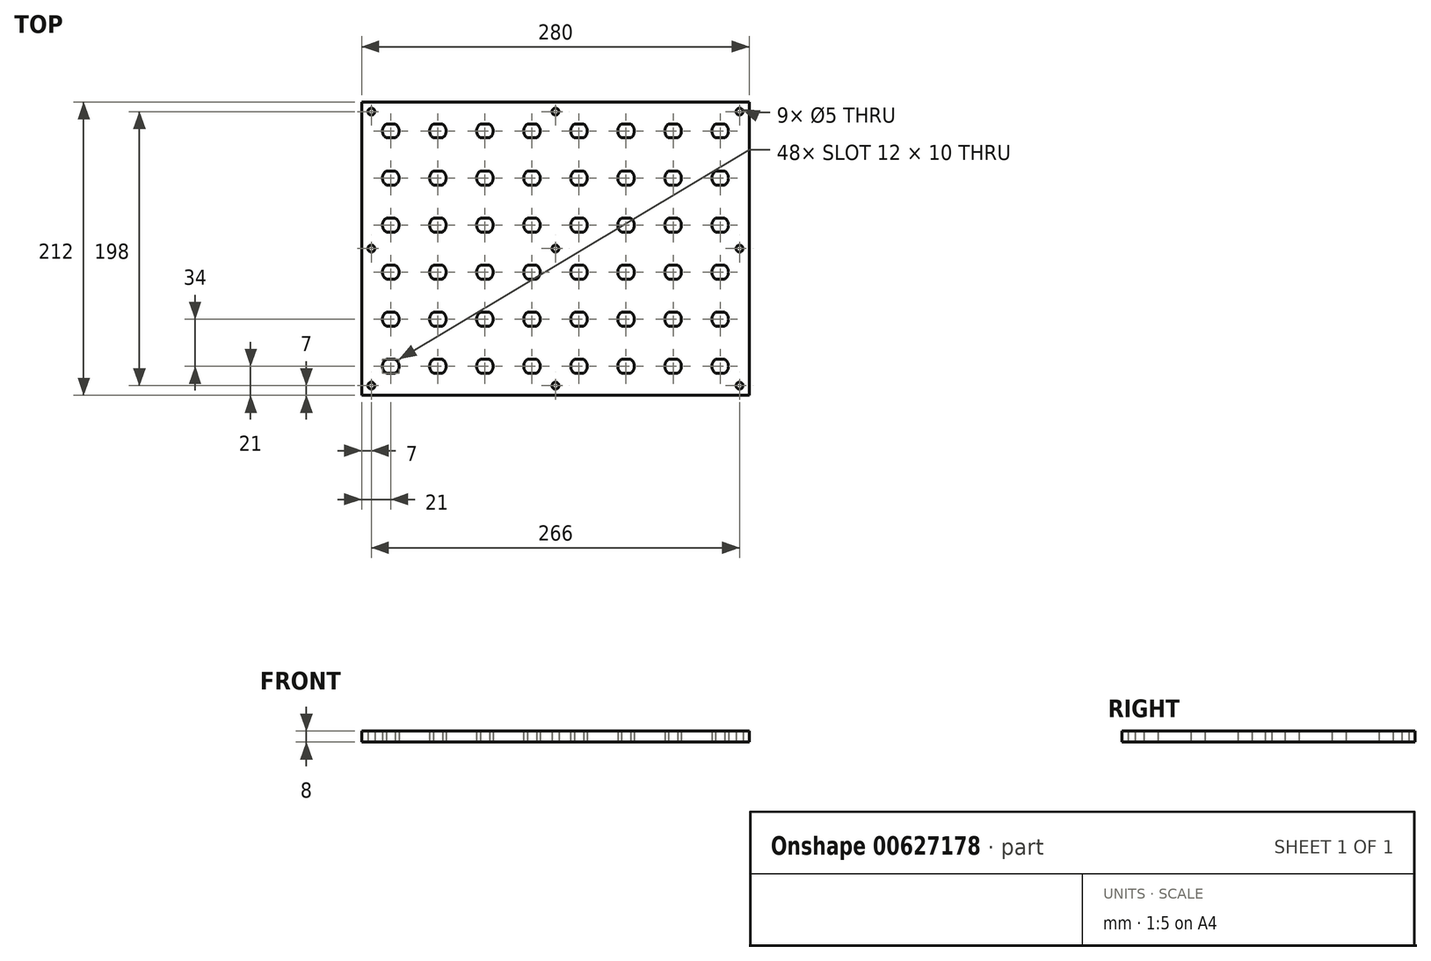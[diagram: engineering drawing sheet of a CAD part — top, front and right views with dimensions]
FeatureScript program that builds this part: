
annotation { "Feature Type Name" : "Feature", "Feature Type Description" : "" }
export const myFeature = defineFeature(function(context is Context, id is Id, definition is map)
    precondition{}
    {
        {
            var Q0;
            Q0=qCreatedBy(makeId("Top.planeOp"),FACE);
            var sketch = newSketch(context, id + "F0", { "sketchPlane" : qUnion([Q0])});
            skLineSegment(sketch, "E0.bottom", {"start": v(-140, -106) * mm, "end": v(140, -106) * mm});
            skLineSegment(sketch, "E0.top", {"start": v(-140, 106) * mm, "end": v(140, 106) * mm});
            skLineSegment(sketch, "E0.left", {"start": v(-140, -106) * mm, "end": v(-140, 106) * mm});
            skLineSegment(sketch, "E0.right", {"start": v(140, -106) * mm, "end": v(140, 106) * mm});
            skPoint(sketch, "E0.middle", {"position": v(0, 0) * mm});
            skLineSegment(sketch, "E1", {"start": v(-102, 141.86) * mm, "end": v(-102, -178.14) * mm, "construction": true});
            skLineSegment(sketch, "E2", {"start": v(-122.32, -80) * mm, "end": v(-115.68, -80) * mm});
            skLineSegment(sketch, "E3", {"start": v(-122.32, -90) * mm, "end": v(-115.68, -90) * mm});
            skArc(sketch, "E4", {"start": v(-122.32, -80) * mm, "mid": v(-125, -85) * mm, "end": v(-122.32, -90) * mm});
            skArc(sketch, "E5", {"start": v(-115.68, -90) * mm, "mid": v(-113, -85) * mm, "end": v(-115.68, -80) * mm});
            skLineSegment(sketch, "E6", {"start": v(-165.76, -85) * mm, "end": v(184.24, -85) * mm, "construction": true});
            skLineSegment(sketch, "E7.0.1.0", {"start": v(-165.76, -51) * mm, "end": v(184.24, -51) * mm, "construction": true});
            skArc(sketch, "E7.0.1.1", {"start": v(-122.32, -46) * mm, "mid": v(-125, -51) * mm, "end": v(-122.32, -56) * mm});
            skLineSegment(sketch, "E7.0.1.2", {"start": v(-122.32, -56) * mm, "end": v(-115.68, -56) * mm});
            skLineSegment(sketch, "E7.0.1.3", {"start": v(-122.32, -46) * mm, "end": v(-115.68, -46) * mm});
            skArc(sketch, "E7.0.1.4", {"start": v(-115.68, -56) * mm, "mid": v(-113, -51) * mm, "end": v(-115.68, -46) * mm});
            skLineSegment(sketch, "E7.0.2.0", {"start": v(-165.76, -17) * mm, "end": v(184.24, -17) * mm, "construction": true});
            skArc(sketch, "E7.0.2.1", {"start": v(-122.32, -12) * mm, "mid": v(-125, -17) * mm, "end": v(-122.32, -22) * mm});
            skLineSegment(sketch, "E7.0.2.2", {"start": v(-122.32, -22) * mm, "end": v(-115.68, -22) * mm});
            skLineSegment(sketch, "E7.0.2.3", {"start": v(-122.32, -12) * mm, "end": v(-115.68, -12) * mm});
            skArc(sketch, "E7.0.2.4", {"start": v(-115.68, -22) * mm, "mid": v(-113, -17) * mm, "end": v(-115.68, -12) * mm});
            skLineSegment(sketch, "E7.0.3.0", {"start": v(-165.76, 17) * mm, "end": v(184.24, 17) * mm, "construction": true});
            skArc(sketch, "E7.0.3.1", {"start": v(-122.32, 22) * mm, "mid": v(-125, 17) * mm, "end": v(-122.32, 12) * mm});
            skLineSegment(sketch, "E7.0.3.2", {"start": v(-122.32, 12) * mm, "end": v(-115.68, 12) * mm});
            skLineSegment(sketch, "E7.0.3.3", {"start": v(-122.32, 22) * mm, "end": v(-115.68, 22) * mm});
            skArc(sketch, "E7.0.3.4", {"start": v(-115.68, 12) * mm, "mid": v(-113, 17) * mm, "end": v(-115.68, 22) * mm});
            skLineSegment(sketch, "E7.0.4.0", {"start": v(-165.76, 51) * mm, "end": v(184.24, 51) * mm, "construction": true});
            skArc(sketch, "E7.0.4.1", {"start": v(-122.32, 56) * mm, "mid": v(-125, 51) * mm, "end": v(-122.32, 46) * mm});
            skLineSegment(sketch, "E7.0.4.2", {"start": v(-122.32, 46) * mm, "end": v(-115.68, 46) * mm});
            skLineSegment(sketch, "E7.0.4.3", {"start": v(-122.32, 56) * mm, "end": v(-115.68, 56) * mm});
            skArc(sketch, "E7.0.4.4", {"start": v(-115.68, 46) * mm, "mid": v(-113, 51) * mm, "end": v(-115.68, 56) * mm});
            skLineSegment(sketch, "E7.1.0.0", {"start": v(-131.76, -85) * mm, "end": v(218.24, -85) * mm, "construction": true});
            skArc(sketch, "E7.1.0.1", {"start": v(-88.32, -80) * mm, "mid": v(-91, -85) * mm, "end": v(-88.32, -90) * mm});
            skLineSegment(sketch, "E7.1.0.2", {"start": v(-88.32, -90) * mm, "end": v(-81.68, -90) * mm});
            skLineSegment(sketch, "E7.1.0.3", {"start": v(-88.32, -80) * mm, "end": v(-81.68, -80) * mm});
            skArc(sketch, "E7.1.0.4", {"start": v(-81.68, -90) * mm, "mid": v(-79, -85) * mm, "end": v(-81.68, -80) * mm});
            skLineSegment(sketch, "E7.1.1.0", {"start": v(-131.76, -51) * mm, "end": v(218.24, -51) * mm, "construction": true});
            skArc(sketch, "E7.1.1.1", {"start": v(-88.32, -46) * mm, "mid": v(-91, -51) * mm, "end": v(-88.32, -56) * mm});
            skLineSegment(sketch, "E7.1.1.2", {"start": v(-88.32, -56) * mm, "end": v(-81.68, -56) * mm});
            skLineSegment(sketch, "E7.1.1.3", {"start": v(-88.32, -46) * mm, "end": v(-81.68, -46) * mm});
            skArc(sketch, "E7.1.1.4", {"start": v(-81.68, -56) * mm, "mid": v(-79, -51) * mm, "end": v(-81.68, -46) * mm});
            skLineSegment(sketch, "E7.1.2.0", {"start": v(-131.76, -17) * mm, "end": v(218.24, -17) * mm, "construction": true});
            skArc(sketch, "E7.1.2.1", {"start": v(-88.32, -12) * mm, "mid": v(-91, -17) * mm, "end": v(-88.32, -22) * mm});
            skLineSegment(sketch, "E7.1.2.2", {"start": v(-88.32, -22) * mm, "end": v(-81.68, -22) * mm});
            skLineSegment(sketch, "E7.1.2.3", {"start": v(-88.32, -12) * mm, "end": v(-81.68, -12) * mm});
            skArc(sketch, "E7.1.2.4", {"start": v(-81.68, -22) * mm, "mid": v(-79, -17) * mm, "end": v(-81.68, -12) * mm});
            skLineSegment(sketch, "E7.1.3.0", {"start": v(-131.76, 17) * mm, "end": v(218.24, 17) * mm, "construction": true});
            skArc(sketch, "E7.1.3.1", {"start": v(-88.32, 22) * mm, "mid": v(-91, 17) * mm, "end": v(-88.32, 12) * mm});
            skLineSegment(sketch, "E7.1.3.2", {"start": v(-88.32, 12) * mm, "end": v(-81.68, 12) * mm});
            skLineSegment(sketch, "E7.1.3.3", {"start": v(-88.32, 22) * mm, "end": v(-81.68, 22) * mm});
            skArc(sketch, "E7.1.3.4", {"start": v(-81.68, 12) * mm, "mid": v(-79, 17) * mm, "end": v(-81.68, 22) * mm});
            skLineSegment(sketch, "E7.1.4.0", {"start": v(-131.76, 51) * mm, "end": v(218.24, 51) * mm, "construction": true});
            skArc(sketch, "E7.1.4.1", {"start": v(-88.32, 56) * mm, "mid": v(-91, 51) * mm, "end": v(-88.32, 46) * mm});
            skLineSegment(sketch, "E7.1.4.2", {"start": v(-88.32, 46) * mm, "end": v(-81.68, 46) * mm});
            skLineSegment(sketch, "E7.1.4.3", {"start": v(-88.32, 56) * mm, "end": v(-81.68, 56) * mm});
            skArc(sketch, "E7.1.4.4", {"start": v(-81.68, 46) * mm, "mid": v(-79, 51) * mm, "end": v(-81.68, 56) * mm});
            skLineSegment(sketch, "E7.2.0.0", {"start": v(-97.76, -85) * mm, "end": v(252.24, -85) * mm, "construction": true});
            skArc(sketch, "E7.2.0.1", {"start": v(-54.32, -80) * mm, "mid": v(-57, -85) * mm, "end": v(-54.32, -90) * mm});
            skLineSegment(sketch, "E7.2.0.2", {"start": v(-54.32, -90) * mm, "end": v(-47.68, -90) * mm});
            skLineSegment(sketch, "E7.2.0.3", {"start": v(-54.32, -80) * mm, "end": v(-47.68, -80) * mm});
            skArc(sketch, "E7.2.0.4", {"start": v(-47.68, -90) * mm, "mid": v(-45, -85) * mm, "end": v(-47.68, -80) * mm});
            skLineSegment(sketch, "E7.2.1.0", {"start": v(-97.76, -51) * mm, "end": v(252.24, -51) * mm, "construction": true});
            skArc(sketch, "E7.2.1.1", {"start": v(-54.32, -46) * mm, "mid": v(-57, -51) * mm, "end": v(-54.32, -56) * mm});
            skLineSegment(sketch, "E7.2.1.2", {"start": v(-54.32, -56) * mm, "end": v(-47.68, -56) * mm});
            skLineSegment(sketch, "E7.2.1.3", {"start": v(-54.32, -46) * mm, "end": v(-47.68, -46) * mm});
            skArc(sketch, "E7.2.1.4", {"start": v(-47.68, -56) * mm, "mid": v(-45, -51) * mm, "end": v(-47.68, -46) * mm});
            skLineSegment(sketch, "E7.2.2.0", {"start": v(-97.76, -17) * mm, "end": v(252.24, -17) * mm, "construction": true});
            skArc(sketch, "E7.2.2.1", {"start": v(-54.32, -12) * mm, "mid": v(-57, -17) * mm, "end": v(-54.32, -22) * mm});
            skLineSegment(sketch, "E7.2.2.2", {"start": v(-54.32, -22) * mm, "end": v(-47.68, -22) * mm});
            skLineSegment(sketch, "E7.2.2.3", {"start": v(-54.32, -12) * mm, "end": v(-47.68, -12) * mm});
            skArc(sketch, "E7.2.2.4", {"start": v(-47.68, -22) * mm, "mid": v(-45, -17) * mm, "end": v(-47.68, -12) * mm});
            skLineSegment(sketch, "E7.2.3.0", {"start": v(-97.76, 17) * mm, "end": v(252.24, 17) * mm, "construction": true});
            skArc(sketch, "E7.2.3.1", {"start": v(-54.32, 22) * mm, "mid": v(-57, 17) * mm, "end": v(-54.32, 12) * mm});
            skLineSegment(sketch, "E7.2.3.2", {"start": v(-54.32, 12) * mm, "end": v(-47.68, 12) * mm});
            skLineSegment(sketch, "E7.2.3.3", {"start": v(-54.32, 22) * mm, "end": v(-47.68, 22) * mm});
            skArc(sketch, "E7.2.3.4", {"start": v(-47.68, 12) * mm, "mid": v(-45, 17) * mm, "end": v(-47.68, 22) * mm});
            skLineSegment(sketch, "E7.2.4.0", {"start": v(-97.76, 51) * mm, "end": v(252.24, 51) * mm, "construction": true});
            skArc(sketch, "E7.2.4.1", {"start": v(-54.32, 56) * mm, "mid": v(-57, 51) * mm, "end": v(-54.32, 46) * mm});
            skLineSegment(sketch, "E7.2.4.2", {"start": v(-54.32, 46) * mm, "end": v(-47.68, 46) * mm});
            skLineSegment(sketch, "E7.2.4.3", {"start": v(-54.32, 56) * mm, "end": v(-47.68, 56) * mm});
            skArc(sketch, "E7.2.4.4", {"start": v(-47.68, 46) * mm, "mid": v(-45, 51) * mm, "end": v(-47.68, 56) * mm});
            skLineSegment(sketch, "E7.3.0.0", {"start": v(-63.76, -85) * mm, "end": v(286.24, -85) * mm, "construction": true});
            skArc(sketch, "E7.3.0.1", {"start": v(-20.32, -80) * mm, "mid": v(-23, -85) * mm, "end": v(-20.32, -90) * mm});
            skLineSegment(sketch, "E7.3.0.2", {"start": v(-20.32, -90) * mm, "end": v(-13.68, -90) * mm});
            skLineSegment(sketch, "E7.3.0.3", {"start": v(-20.32, -80) * mm, "end": v(-13.68, -80) * mm});
            skArc(sketch, "E7.3.0.4", {"start": v(-13.68, -90) * mm, "mid": v(-11, -85) * mm, "end": v(-13.68, -80) * mm});
            skLineSegment(sketch, "E7.3.1.0", {"start": v(-63.76, -51) * mm, "end": v(286.24, -51) * mm, "construction": true});
            skArc(sketch, "E7.3.1.1", {"start": v(-20.32, -46) * mm, "mid": v(-23, -51) * mm, "end": v(-20.32, -56) * mm});
            skLineSegment(sketch, "E7.3.1.2", {"start": v(-20.32, -56) * mm, "end": v(-13.68, -56) * mm});
            skLineSegment(sketch, "E7.3.1.3", {"start": v(-20.32, -46) * mm, "end": v(-13.68, -46) * mm});
            skArc(sketch, "E7.3.1.4", {"start": v(-13.68, -56) * mm, "mid": v(-11, -51) * mm, "end": v(-13.68, -46) * mm});
            skLineSegment(sketch, "E7.3.2.0", {"start": v(-63.76, -17) * mm, "end": v(286.24, -17) * mm, "construction": true});
            skArc(sketch, "E7.3.2.1", {"start": v(-20.32, -12) * mm, "mid": v(-23, -17) * mm, "end": v(-20.32, -22) * mm});
            skLineSegment(sketch, "E7.3.2.2", {"start": v(-20.32, -22) * mm, "end": v(-13.68, -22) * mm});
            skLineSegment(sketch, "E7.3.2.3", {"start": v(-20.32, -12) * mm, "end": v(-13.68, -12) * mm});
            skArc(sketch, "E7.3.2.4", {"start": v(-13.68, -22) * mm, "mid": v(-11, -17) * mm, "end": v(-13.68, -12) * mm});
            skLineSegment(sketch, "E7.3.3.0", {"start": v(-63.76, 17) * mm, "end": v(286.24, 17) * mm, "construction": true});
            skArc(sketch, "E7.3.3.1", {"start": v(-20.32, 22) * mm, "mid": v(-23, 17) * mm, "end": v(-20.32, 12) * mm});
            skLineSegment(sketch, "E7.3.3.2", {"start": v(-20.32, 12) * mm, "end": v(-13.68, 12) * mm});
            skLineSegment(sketch, "E7.3.3.3", {"start": v(-20.32, 22) * mm, "end": v(-13.68, 22) * mm});
            skArc(sketch, "E7.3.3.4", {"start": v(-13.68, 12) * mm, "mid": v(-11, 17) * mm, "end": v(-13.68, 22) * mm});
            skLineSegment(sketch, "E7.3.4.0", {"start": v(-63.76, 51) * mm, "end": v(286.24, 51) * mm, "construction": true});
            skArc(sketch, "E7.3.4.1", {"start": v(-20.32, 56) * mm, "mid": v(-23, 51) * mm, "end": v(-20.32, 46) * mm});
            skLineSegment(sketch, "E7.3.4.2", {"start": v(-20.32, 46) * mm, "end": v(-13.68, 46) * mm});
            skLineSegment(sketch, "E7.3.4.3", {"start": v(-20.32, 56) * mm, "end": v(-13.68, 56) * mm});
            skArc(sketch, "E7.3.4.4", {"start": v(-13.68, 46) * mm, "mid": v(-11, 51) * mm, "end": v(-13.68, 56) * mm});
            skLineSegment(sketch, "E7.4.0.0", {"start": v(-29.76, -85) * mm, "end": v(320.24, -85) * mm, "construction": true});
            skArc(sketch, "E7.4.0.1", {"start": v(13.68, -80) * mm, "mid": v(11, -85) * mm, "end": v(13.68, -90) * mm});
            skLineSegment(sketch, "E7.4.0.2", {"start": v(13.68, -90) * mm, "end": v(20.32, -90) * mm});
            skLineSegment(sketch, "E7.4.0.3", {"start": v(13.68, -80) * mm, "end": v(20.32, -80) * mm});
            skArc(sketch, "E7.4.0.4", {"start": v(20.32, -90) * mm, "mid": v(23, -85) * mm, "end": v(20.32, -80) * mm});
            skLineSegment(sketch, "E7.4.1.0", {"start": v(-29.76, -51) * mm, "end": v(320.24, -51) * mm, "construction": true});
            skArc(sketch, "E7.4.1.1", {"start": v(13.68, -46) * mm, "mid": v(11, -51) * mm, "end": v(13.68, -56) * mm});
            skLineSegment(sketch, "E7.4.1.2", {"start": v(13.68, -56) * mm, "end": v(20.32, -56) * mm});
            skLineSegment(sketch, "E7.4.1.3", {"start": v(13.68, -46) * mm, "end": v(20.32, -46) * mm});
            skArc(sketch, "E7.4.1.4", {"start": v(20.32, -56) * mm, "mid": v(23, -51) * mm, "end": v(20.32, -46) * mm});
            skLineSegment(sketch, "E7.4.2.0", {"start": v(-29.76, -17) * mm, "end": v(320.24, -17) * mm, "construction": true});
            skArc(sketch, "E7.4.2.1", {"start": v(13.68, -12) * mm, "mid": v(11, -17) * mm, "end": v(13.68, -22) * mm});
            skLineSegment(sketch, "E7.4.2.2", {"start": v(13.68, -22) * mm, "end": v(20.32, -22) * mm});
            skLineSegment(sketch, "E7.4.2.3", {"start": v(13.68, -12) * mm, "end": v(20.32, -12) * mm});
            skArc(sketch, "E7.4.2.4", {"start": v(20.32, -22) * mm, "mid": v(23, -17) * mm, "end": v(20.32, -12) * mm});
            skLineSegment(sketch, "E7.4.3.0", {"start": v(-29.76, 17) * mm, "end": v(320.24, 17) * mm, "construction": true});
            skArc(sketch, "E7.4.3.1", {"start": v(13.68, 22) * mm, "mid": v(11, 17) * mm, "end": v(13.68, 12) * mm});
            skLineSegment(sketch, "E7.4.3.2", {"start": v(13.68, 12) * mm, "end": v(20.32, 12) * mm});
            skLineSegment(sketch, "E7.4.3.3", {"start": v(13.68, 22) * mm, "end": v(20.32, 22) * mm});
            skArc(sketch, "E7.4.3.4", {"start": v(20.32, 12) * mm, "mid": v(23, 17) * mm, "end": v(20.32, 22) * mm});
            skLineSegment(sketch, "E7.4.4.0", {"start": v(-29.76, 51) * mm, "end": v(320.24, 51) * mm, "construction": true});
            skArc(sketch, "E7.4.4.1", {"start": v(13.68, 56) * mm, "mid": v(11, 51) * mm, "end": v(13.68, 46) * mm});
            skLineSegment(sketch, "E7.4.4.2", {"start": v(13.68, 46) * mm, "end": v(20.32, 46) * mm});
            skLineSegment(sketch, "E7.4.4.3", {"start": v(13.68, 56) * mm, "end": v(20.32, 56) * mm});
            skArc(sketch, "E7.4.4.4", {"start": v(20.32, 46) * mm, "mid": v(23, 51) * mm, "end": v(20.32, 56) * mm});
            skLineSegment(sketch, "E7.5.0.0", {"start": v(4.24, -85) * mm, "end": v(354.24, -85) * mm, "construction": true});
            skArc(sketch, "E7.5.0.1", {"start": v(47.68, -80) * mm, "mid": v(45, -85) * mm, "end": v(47.68, -90) * mm});
            skLineSegment(sketch, "E7.5.0.2", {"start": v(47.68, -90) * mm, "end": v(54.32, -90) * mm});
            skLineSegment(sketch, "E7.5.0.3", {"start": v(47.68, -80) * mm, "end": v(54.32, -80) * mm});
            skArc(sketch, "E7.5.0.4", {"start": v(54.32, -90) * mm, "mid": v(57, -85) * mm, "end": v(54.32, -80) * mm});
            skLineSegment(sketch, "E7.5.1.0", {"start": v(4.24, -51) * mm, "end": v(354.24, -51) * mm, "construction": true});
            skArc(sketch, "E7.5.1.1", {"start": v(47.68, -46) * mm, "mid": v(45, -51) * mm, "end": v(47.68, -56) * mm});
            skLineSegment(sketch, "E7.5.1.2", {"start": v(47.68, -56) * mm, "end": v(54.32, -56) * mm});
            skLineSegment(sketch, "E7.5.1.3", {"start": v(47.68, -46) * mm, "end": v(54.32, -46) * mm});
            skArc(sketch, "E7.5.1.4", {"start": v(54.32, -56) * mm, "mid": v(57, -51) * mm, "end": v(54.32, -46) * mm});
            skLineSegment(sketch, "E7.5.2.0", {"start": v(4.24, -17) * mm, "end": v(354.24, -17) * mm, "construction": true});
            skArc(sketch, "E7.5.2.1", {"start": v(47.68, -12) * mm, "mid": v(45, -17) * mm, "end": v(47.68, -22) * mm});
            skLineSegment(sketch, "E7.5.2.2", {"start": v(47.68, -22) * mm, "end": v(54.32, -22) * mm});
            skLineSegment(sketch, "E7.5.2.3", {"start": v(47.68, -12) * mm, "end": v(54.32, -12) * mm});
            skArc(sketch, "E7.5.2.4", {"start": v(54.32, -22) * mm, "mid": v(57, -17) * mm, "end": v(54.32, -12) * mm});
            skLineSegment(sketch, "E7.5.3.0", {"start": v(4.24, 17) * mm, "end": v(354.24, 17) * mm, "construction": true});
            skArc(sketch, "E7.5.3.1", {"start": v(47.68, 22) * mm, "mid": v(45, 17) * mm, "end": v(47.68, 12) * mm});
            skLineSegment(sketch, "E7.5.3.2", {"start": v(47.68, 12) * mm, "end": v(54.32, 12) * mm});
            skLineSegment(sketch, "E7.5.3.3", {"start": v(47.68, 22) * mm, "end": v(54.32, 22) * mm});
            skArc(sketch, "E7.5.3.4", {"start": v(54.32, 12) * mm, "mid": v(57, 17) * mm, "end": v(54.32, 22) * mm});
            skLineSegment(sketch, "E7.5.4.0", {"start": v(4.24, 51) * mm, "end": v(354.24, 51) * mm, "construction": true});
            skArc(sketch, "E7.5.4.1", {"start": v(47.68, 56) * mm, "mid": v(45, 51) * mm, "end": v(47.68, 46) * mm});
            skLineSegment(sketch, "E7.5.4.2", {"start": v(47.68, 46) * mm, "end": v(54.32, 46) * mm});
            skLineSegment(sketch, "E7.5.4.3", {"start": v(47.68, 56) * mm, "end": v(54.32, 56) * mm});
            skArc(sketch, "E7.5.4.4", {"start": v(54.32, 46) * mm, "mid": v(57, 51) * mm, "end": v(54.32, 56) * mm});
            skLineSegment(sketch, "E7.6.0.0", {"start": v(38.24, -85) * mm, "end": v(388.24, -85) * mm, "construction": true});
            skArc(sketch, "E7.6.0.1", {"start": v(81.68, -80) * mm, "mid": v(79, -85) * mm, "end": v(81.68, -90) * mm});
            skLineSegment(sketch, "E7.6.0.2", {"start": v(81.68, -90) * mm, "end": v(88.32, -90) * mm});
            skLineSegment(sketch, "E7.6.0.3", {"start": v(81.68, -80) * mm, "end": v(88.32, -80) * mm});
            skArc(sketch, "E7.6.0.4", {"start": v(88.32, -90) * mm, "mid": v(91, -85) * mm, "end": v(88.32, -80) * mm});
            skLineSegment(sketch, "E7.6.1.0", {"start": v(38.24, -51) * mm, "end": v(388.24, -51) * mm, "construction": true});
            skArc(sketch, "E7.6.1.1", {"start": v(81.68, -46) * mm, "mid": v(79, -51) * mm, "end": v(81.68, -56) * mm});
            skLineSegment(sketch, "E7.6.1.2", {"start": v(81.68, -56) * mm, "end": v(88.32, -56) * mm});
            skLineSegment(sketch, "E7.6.1.3", {"start": v(81.68, -46) * mm, "end": v(88.32, -46) * mm});
            skArc(sketch, "E7.6.1.4", {"start": v(88.32, -56) * mm, "mid": v(91, -51) * mm, "end": v(88.32, -46) * mm});
            skLineSegment(sketch, "E7.6.2.0", {"start": v(38.24, -17) * mm, "end": v(388.24, -17) * mm, "construction": true});
            skArc(sketch, "E7.6.2.1", {"start": v(81.68, -12) * mm, "mid": v(79, -17) * mm, "end": v(81.68, -22) * mm});
            skLineSegment(sketch, "E7.6.2.2", {"start": v(81.68, -22) * mm, "end": v(88.32, -22) * mm});
            skLineSegment(sketch, "E7.6.2.3", {"start": v(81.68, -12) * mm, "end": v(88.32, -12) * mm});
            skArc(sketch, "E7.6.2.4", {"start": v(88.32, -22) * mm, "mid": v(91, -17) * mm, "end": v(88.32, -12) * mm});
            skLineSegment(sketch, "E7.6.3.0", {"start": v(38.24, 17) * mm, "end": v(388.24, 17) * mm, "construction": true});
            skArc(sketch, "E7.6.3.1", {"start": v(81.68, 22) * mm, "mid": v(79, 17) * mm, "end": v(81.68, 12) * mm});
            skLineSegment(sketch, "E7.6.3.2", {"start": v(81.68, 12) * mm, "end": v(88.32, 12) * mm});
            skLineSegment(sketch, "E7.6.3.3", {"start": v(81.68, 22) * mm, "end": v(88.32, 22) * mm});
            skArc(sketch, "E7.6.3.4", {"start": v(88.32, 12) * mm, "mid": v(91, 17) * mm, "end": v(88.32, 22) * mm});
            skLineSegment(sketch, "E7.6.4.0", {"start": v(38.24, 51) * mm, "end": v(388.24, 51) * mm, "construction": true});
            skArc(sketch, "E7.6.4.1", {"start": v(81.68, 56) * mm, "mid": v(79, 51) * mm, "end": v(81.68, 46) * mm});
            skLineSegment(sketch, "E7.6.4.2", {"start": v(81.68, 46) * mm, "end": v(88.32, 46) * mm});
            skLineSegment(sketch, "E7.6.4.3", {"start": v(81.68, 56) * mm, "end": v(88.32, 56) * mm});
            skArc(sketch, "E7.6.4.4", {"start": v(88.32, 46) * mm, "mid": v(91, 51) * mm, "end": v(88.32, 56) * mm});
            skArc(sketch, "E7.7.0.1", {"start": v(115.68, -80) * mm, "mid": v(113, -85) * mm, "end": v(115.68, -90) * mm});
            skLineSegment(sketch, "E7.7.0.2", {"start": v(115.68, -90) * mm, "end": v(122.32, -90) * mm});
            skLineSegment(sketch, "E7.7.0.3", {"start": v(115.68, -80) * mm, "end": v(122.32, -80) * mm});
            skArc(sketch, "E7.7.0.4", {"start": v(122.32, -90) * mm, "mid": v(125, -85) * mm, "end": v(122.32, -80) * mm});
            skArc(sketch, "E7.7.1.1", {"start": v(115.68, -46) * mm, "mid": v(113, -51) * mm, "end": v(115.68, -56) * mm});
            skLineSegment(sketch, "E7.7.1.2", {"start": v(115.68, -56) * mm, "end": v(122.32, -56) * mm});
            skLineSegment(sketch, "E7.7.1.3", {"start": v(115.68, -46) * mm, "end": v(122.32, -46) * mm});
            skArc(sketch, "E7.7.1.4", {"start": v(122.32, -56) * mm, "mid": v(125, -51) * mm, "end": v(122.32, -46) * mm});
            skArc(sketch, "E7.7.2.1", {"start": v(115.68, -12) * mm, "mid": v(113, -17) * mm, "end": v(115.68, -22) * mm});
            skLineSegment(sketch, "E7.7.2.2", {"start": v(115.68, -22) * mm, "end": v(122.32, -22) * mm});
            skLineSegment(sketch, "E7.7.2.3", {"start": v(115.68, -12) * mm, "end": v(122.32, -12) * mm});
            skArc(sketch, "E7.7.2.4", {"start": v(122.32, -22) * mm, "mid": v(125, -17) * mm, "end": v(122.32, -12) * mm});
            skArc(sketch, "E7.7.3.1", {"start": v(115.68, 22) * mm, "mid": v(113, 17) * mm, "end": v(115.68, 12) * mm});
            skLineSegment(sketch, "E7.7.3.2", {"start": v(115.68, 12) * mm, "end": v(122.32, 12) * mm});
            skLineSegment(sketch, "E7.7.3.3", {"start": v(115.68, 22) * mm, "end": v(122.32, 22) * mm});
            skArc(sketch, "E7.7.3.4", {"start": v(122.32, 12) * mm, "mid": v(125, 17) * mm, "end": v(122.32, 22) * mm});
            skArc(sketch, "E7.7.4.1", {"start": v(115.68, 56) * mm, "mid": v(113, 51) * mm, "end": v(115.68, 46) * mm});
            skLineSegment(sketch, "E7.7.4.2", {"start": v(115.68, 46) * mm, "end": v(122.32, 46) * mm});
            skLineSegment(sketch, "E7.7.4.3", {"start": v(115.68, 56) * mm, "end": v(122.32, 56) * mm});
            skArc(sketch, "E7.7.4.4", {"start": v(122.32, 46) * mm, "mid": v(125, 51) * mm, "end": v(122.32, 56) * mm});
            skLineSegment(sketch, "E7.direction1", {"start": v(-165.76, -85) * mm, "end": v(-131.76, -85) * mm, "construction": true});
            skLineSegment(sketch, "E7.direction2", {"start": v(-165.76, -85) * mm, "end": v(-165.76, -51) * mm, "construction": true});
            skLineSegment(sketch, "E8.0.0.5", {"start": v(-165.76, 85) * mm, "end": v(184.24, 85) * mm, "construction": true});
            skArc(sketch, "E8.3.0.5", {"start": v(-122.32, 90) * mm, "mid": v(-125, 85) * mm, "end": v(-122.32, 80) * mm});
            skLineSegment(sketch, "E8.7.0.5", {"start": v(-122.32, 80) * mm, "end": v(-115.68, 80) * mm});
            skLineSegment(sketch, "E8.10.0.5", {"start": v(-122.32, 90) * mm, "end": v(-115.68, 90) * mm});
            skArc(sketch, "E8.13.0.5", {"start": v(-115.68, 80) * mm, "mid": v(-113, 85) * mm, "end": v(-115.68, 90) * mm});
            skLineSegment(sketch, "E8.0.1.5", {"start": v(-131.76, 85) * mm, "end": v(218.24, 85) * mm, "construction": true});
            skArc(sketch, "E8.3.1.5", {"start": v(-88.32, 90) * mm, "mid": v(-91, 85) * mm, "end": v(-88.32, 80) * mm});
            skLineSegment(sketch, "E8.7.1.5", {"start": v(-88.32, 80) * mm, "end": v(-81.68, 80) * mm});
            skLineSegment(sketch, "E8.10.1.5", {"start": v(-88.32, 90) * mm, "end": v(-81.68, 90) * mm});
            skArc(sketch, "E8.13.1.5", {"start": v(-81.68, 80) * mm, "mid": v(-79, 85) * mm, "end": v(-81.68, 90) * mm});
            skLineSegment(sketch, "E8.0.2.5", {"start": v(-97.76, 85) * mm, "end": v(252.24, 85) * mm, "construction": true});
            skArc(sketch, "E8.3.2.5", {"start": v(-54.32, 90) * mm, "mid": v(-57, 85) * mm, "end": v(-54.32, 80) * mm});
            skLineSegment(sketch, "E8.7.2.5", {"start": v(-54.32, 80) * mm, "end": v(-47.68, 80) * mm});
            skLineSegment(sketch, "E8.10.2.5", {"start": v(-54.32, 90) * mm, "end": v(-47.68, 90) * mm});
            skArc(sketch, "E8.13.2.5", {"start": v(-47.68, 80) * mm, "mid": v(-45, 85) * mm, "end": v(-47.68, 90) * mm});
            skLineSegment(sketch, "E8.0.3.5", {"start": v(-63.76, 85) * mm, "end": v(286.24, 85) * mm, "construction": true});
            skArc(sketch, "E8.3.3.5", {"start": v(-20.32, 90) * mm, "mid": v(-23, 85) * mm, "end": v(-20.32, 80) * mm});
            skLineSegment(sketch, "E8.7.3.5", {"start": v(-20.32, 80) * mm, "end": v(-13.68, 80) * mm});
            skLineSegment(sketch, "E8.10.3.5", {"start": v(-20.32, 90) * mm, "end": v(-13.68, 90) * mm});
            skArc(sketch, "E8.13.3.5", {"start": v(-13.68, 80) * mm, "mid": v(-11, 85) * mm, "end": v(-13.68, 90) * mm});
            skLineSegment(sketch, "E8.0.4.5", {"start": v(-29.76, 85) * mm, "end": v(320.24, 85) * mm, "construction": true});
            skArc(sketch, "E8.3.4.5", {"start": v(13.68, 90) * mm, "mid": v(11, 85) * mm, "end": v(13.68, 80) * mm});
            skLineSegment(sketch, "E8.7.4.5", {"start": v(13.68, 80) * mm, "end": v(20.32, 80) * mm});
            skLineSegment(sketch, "E8.10.4.5", {"start": v(13.68, 90) * mm, "end": v(20.32, 90) * mm});
            skArc(sketch, "E8.13.4.5", {"start": v(20.32, 80) * mm, "mid": v(23, 85) * mm, "end": v(20.32, 90) * mm});
            skLineSegment(sketch, "E8.0.5.5", {"start": v(4.24, 85) * mm, "end": v(354.24, 85) * mm, "construction": true});
            skArc(sketch, "E8.3.5.5", {"start": v(47.68, 90) * mm, "mid": v(45, 85) * mm, "end": v(47.68, 80) * mm});
            skLineSegment(sketch, "E8.7.5.5", {"start": v(47.68, 80) * mm, "end": v(54.32, 80) * mm});
            skLineSegment(sketch, "E8.10.5.5", {"start": v(47.68, 90) * mm, "end": v(54.32, 90) * mm});
            skArc(sketch, "E8.13.5.5", {"start": v(54.32, 80) * mm, "mid": v(57, 85) * mm, "end": v(54.32, 90) * mm});
            skLineSegment(sketch, "E8.0.6.5", {"start": v(38.24, 85) * mm, "end": v(388.24, 85) * mm, "construction": true});
            skArc(sketch, "E8.3.6.5", {"start": v(81.68, 90) * mm, "mid": v(79, 85) * mm, "end": v(81.68, 80) * mm});
            skLineSegment(sketch, "E8.7.6.5", {"start": v(81.68, 80) * mm, "end": v(88.32, 80) * mm});
            skLineSegment(sketch, "E8.10.6.5", {"start": v(81.68, 90) * mm, "end": v(88.32, 90) * mm});
            skArc(sketch, "E8.13.6.5", {"start": v(88.32, 80) * mm, "mid": v(91, 85) * mm, "end": v(88.32, 90) * mm});
            skLineSegment(sketch, "E8.0.7.5", {"start": v(72.24, 85) * mm, "end": v(422.24, 85) * mm, "construction": true});
            skArc(sketch, "E8.3.7.5", {"start": v(115.68, 90) * mm, "mid": v(113, 85) * mm, "end": v(115.68, 80) * mm});
            skLineSegment(sketch, "E8.7.7.5", {"start": v(115.68, 80) * mm, "end": v(122.32, 80) * mm});
            skLineSegment(sketch, "E8.10.7.5", {"start": v(115.68, 90) * mm, "end": v(122.32, 90) * mm});
            skArc(sketch, "E8.13.7.5", {"start": v(122.32, 80) * mm, "mid": v(125, 85) * mm, "end": v(122.32, 90) * mm});
            skCircle(sketch, "E9", {"center": v(133, -99) * mm, "radius": 2.5 * mm});
            skCircle(sketch, "E10.0.1.0", {"center": v(133, 0) * mm, "radius": 2.5 * mm});
            skCircle(sketch, "E10.0.2.0", {"center": v(133, 99) * mm, "radius": 2.5 * mm});
            skCircle(sketch, "E10.1.0.0", {"center": v(0, -99) * mm, "radius": 2.5 * mm});
            skCircle(sketch, "E10.1.1.0", {"center": v(0, 0) * mm, "radius": 2.5 * mm});
            skCircle(sketch, "E10.1.2.0", {"center": v(0, 99) * mm, "radius": 2.5 * mm});
            skCircle(sketch, "E10.2.0.0", {"center": v(-133, -99) * mm, "radius": 2.5 * mm});
            skCircle(sketch, "E10.2.1.0", {"center": v(-133, 0) * mm, "radius": 2.5 * mm});
            skCircle(sketch, "E10.2.2.0", {"center": v(-133, 99) * mm, "radius": 2.5 * mm});
            skLineSegment(sketch, "E10.direction1", {"start": v(133, -99) * mm, "end": v(0, -99) * mm, "construction": true});
            skLineSegment(sketch, "E10.direction2", {"start": v(133, -99) * mm, "end": v(133, 0) * mm, "construction": true});
            skSolve(sketch);
        }
        {
            var Q0;
            Q0=makeQuery(id+"F0.imprint","IMPRINT",FACE,{"disambiguationData":[TD([[makeQuery(id+"F0.imprint","IMPRINT",EDGE,{"derivedFrom":sQuery(id+"F0.wireOp",EDGE,"E0.bottom")}),1.0]])]});
            extrude(context, id + "F1", {"entities" : qUnion([Q0]), "depth" : 8 * mm, "offsetDistance" : 25 * mm});
        }
    });
